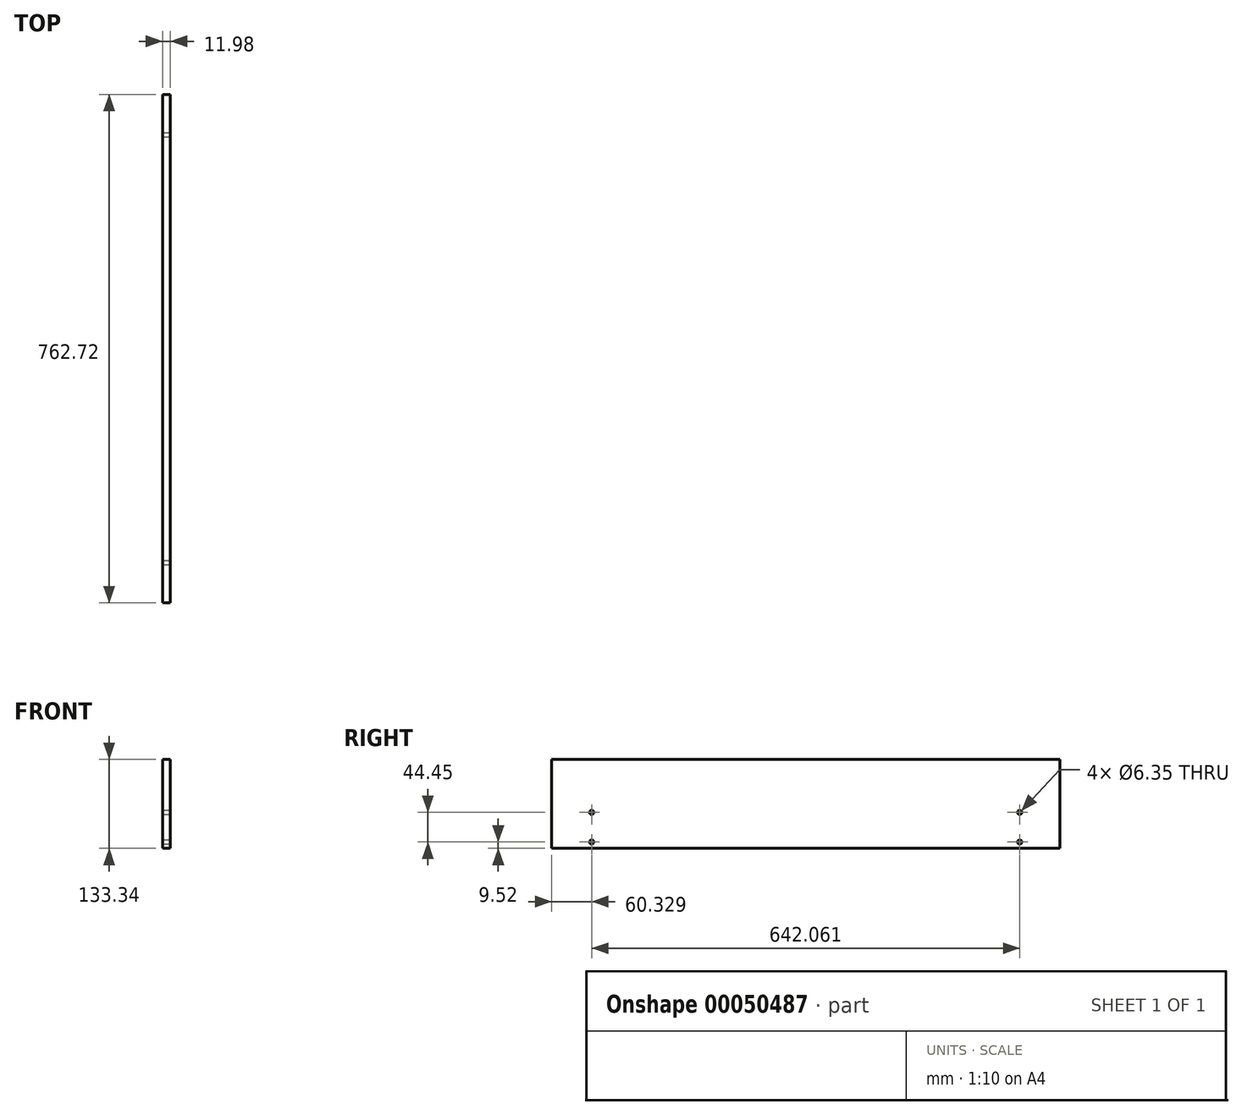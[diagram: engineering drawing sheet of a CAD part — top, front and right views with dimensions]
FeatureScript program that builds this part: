
annotation { "Feature Type Name" : "Feature", "Feature Type Description" : "" }
export const myFeature = defineFeature(function(context is Context, id is Id, definition is map)
    precondition{}
    {
        {
            var Q0;
            Q0=qCreatedBy(makeId("Right.planeOp"),FACE);
            var sketch = newSketch(context, id + "F0", { "sketchPlane" : qUnion([Q0])});
            skLineSegment(sketch, "E0.rect.bottom", {"start": v(381.36, -66.67) * mm, "end": v(-381.36, -66.67) * mm});
            skLineSegment(sketch, "E0.rect.top", {"start": v(381.36, 66.68) * mm, "end": v(-381.36, 66.67) * mm});
            skLineSegment(sketch, "E0.rect.left", {"start": v(381.36, -66.67) * mm, "end": v(381.36, 66.68) * mm});
            skLineSegment(sketch, "E0.rect.right", {"start": v(-381.36, -66.67) * mm, "end": v(-381.36, 66.68) * mm});
            skPoint(sketch, "E0.rect.middle", {"position": v(0, 0) * mm});
            skSolve(sketch);
        }
        {
            var Q0;
            Q0=qSketchRegion(id+"F0",true);
            extrude(context, id + "F1", {"entities" : qUnion([Q0]), "endBound" : BoundingType.SYMMETRIC, "depth" : 12 * mm});
        }
        {
            var Q0;
            Q0=makeQuery(id+"F1.opExtrude","CAP_FACE",FACE,{"disambiguationData":[OSD([sQuery(id+"F0.wireOp",EDGE,"E0.rect.bottom"),sQuery(id+"F0.wireOp",EDGE,"E0.rect.top"),sQuery(id+"F0.wireOp",EDGE,"E0.rect.left"),sQuery(id+"F0.wireOp",EDGE,"E0.rect.right")])],"isStart":false});
            var sketch = newSketch(context, id + "F2", { "sketchPlane" : qUnion([Q0])});
            skLineSegment(sketch, "E1.bottom", {"start": v(-321.03, -12.7) * mm, "end": v(321.03, -12.7) * mm, "construction": true});
            skLineSegment(sketch, "E1.top", {"start": v(-321.03, -57.15) * mm, "end": v(321.03, -57.15) * mm, "construction": true});
            skLineSegment(sketch, "E1.left", {"start": v(-321.03, -12.7) * mm, "end": v(-321.03, -57.15) * mm, "construction": true});
            skLineSegment(sketch, "E1.right", {"start": v(321.03, -12.7) * mm, "end": v(321.03, -57.15) * mm, "construction": true});
            skCircle(sketch, "E2", {"center": v(-321.03, -12.7) * mm, "radius": 3.18 * mm});
            skCircle(sketch, "E3", {"center": v(-321.03, -57.15) * mm, "radius": 3.18 * mm});
            skCircle(sketch, "E4", {"center": v(321.03, -57.15) * mm, "radius": 3.18 * mm});
            skCircle(sketch, "E5", {"center": v(321.03, -12.7) * mm, "radius": 3.18 * mm});
            skSolve(sketch);
        }
        {
            var Q0;
            Q0 = qSketchRegion(id + "F2", true);
            extrude(context, id + "F3", {"entities" : qUnion([Q0]), "operationType" : NewBodyOperationType.REMOVE, "endBound" : BoundingType.UP_TO_NEXT, "oppositeDirection" : true, "depth" : 25.4 * mm});
        }
    });
